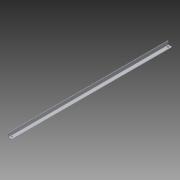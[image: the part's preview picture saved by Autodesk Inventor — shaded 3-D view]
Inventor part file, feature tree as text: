
AUTODESK INVENTOR PART (.ipt)
format: ipt  version: 2014 (Build 180170000, 170)  size: 96,256 bytes
history: native  units: in
note: dims shown in document units (in); Inventor stores cm internally (conversion verified against a paired STEP export)
features: extrude x2, sketch x2, fillet x1, projected_geometry x1
ambient origin geometry x8: Origin, YZ Plane, XZ Plane, XY Plane, X Axis, Y Axis, Z Axis, Center Point
bodies: Solid1 (feature_tree)
feature tree (6):
  extrude  "Extrusion1"  Depth=0.05in
  fillet  "Fillet1"  Radius=0.45in
  extrude  "Extrusion2"  Depth=0.05in
  sketch  "Sketch1"  dims[d0=0.5in d1=0.05in d2=0.45in]
  sketch  "Sketch2"  dims[d3=20.0in d4=0.0in d5=0.05in d6=0.196in d7=0.25in d8=0.25in d9=1.0in d10=0.0in]
  projected_geometry  "Projected Loop1"
